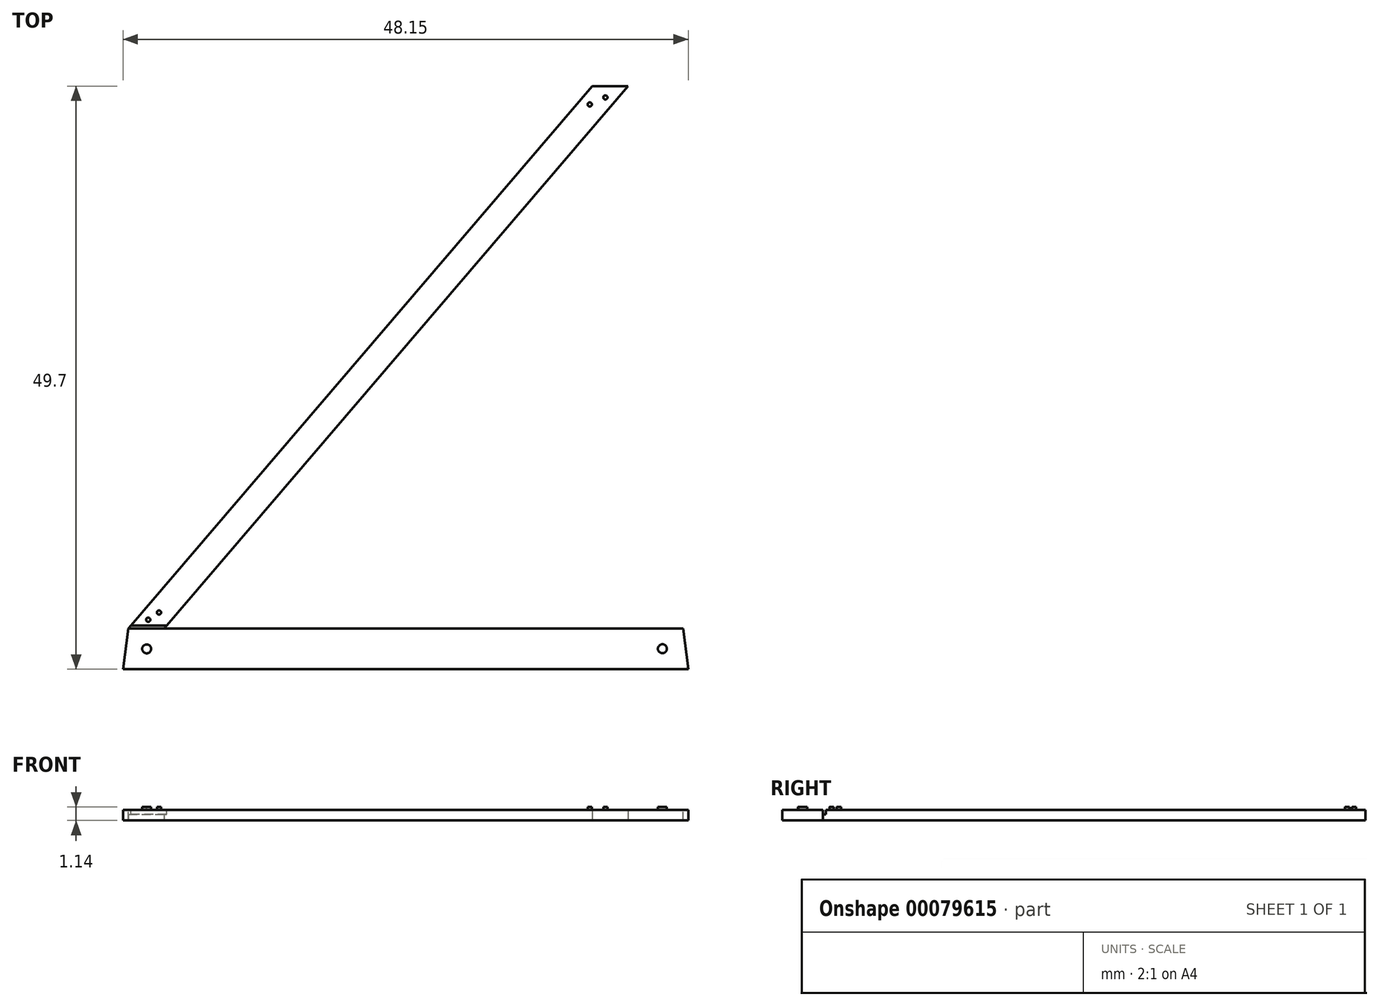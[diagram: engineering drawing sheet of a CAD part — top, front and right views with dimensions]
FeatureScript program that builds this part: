
annotation { "Feature Type Name" : "Feature", "Feature Type Description" : "" }
export const myFeature = defineFeature(function(context is Context, id is Id, definition is map)
    precondition{}
    {
        {
            var Q0;
            Q0=qCreatedBy(makeId("Top.planeOp"),FACE);
            var sketch = newSketch(context, id + "F0", { "sketchPlane" : qUnion([Q0])});
            skLineSegment(sketch, "E0.bottom", {"start": v(-26.81, -12.22) * mm, "end": v(-24.95, -12.22) * mm});
            skLineSegment(sketch, "E0.top", {"start": v(-26.81, -15.7) * mm, "end": v(23.99, -15.7) * mm});
            skLineSegment(sketch, "E0.left", {"start": v(-26.81, -12.22) * mm, "end": v(-26.81, -15.7) * mm});
            skLineSegment(sketch, "E0.right", {"start": v(23.99, -12.22) * mm, "end": v(23.99, -15.7) * mm});
            skLineSegment(sketch, "E1", {"start": v(-24.95, -12.22) * mm, "end": v(14.59, 34.01) * mm});
            skLineSegment(sketch, "E2", {"start": v(-21.9, -12.22) * mm, "end": v(17.64, 34.01) * mm});
            skLineSegment(sketch, "E3", {"start": v(14.59, 34.01) * mm, "end": v(17.64, 34.01) * mm});
            skLineSegment(sketch, "E4.trimOffspring", {"start": v(-21.9, -12.22) * mm, "end": v(23.99, -12.22) * mm});
            skSolve(sketch);
        }
        {
            var Q0;
            Q0=qSketchRegion(id+"F0",true);
            extrude(context, id + "F1", {"entities" : qUnion([Q0]), "depth" : 0.89 * mm});
        }
        {
            var Q0;
            Q0=makeQuery(id+"F1.opExtrude","CAP_FACE",FACE,{"disambiguationData":[OSD([sQuery(id+"F0.wireOp",EDGE,"E0.bottom"),sQuery(id+"F0.wireOp",EDGE,"E0.top"),sQuery(id+"F0.wireOp",EDGE,"E0.left"),sQuery(id+"F0.wireOp",EDGE,"E0.right"),sQuery(id+"F0.wireOp",EDGE,"E1"),sQuery(id+"F0.wireOp",EDGE,"E2"),sQuery(id+"F0.wireOp",EDGE,"E3"),sQuery(id+"F0.wireOp",EDGE,"E4.trimOffspring")])],"isStart":false});
            var sketch = newSketch(context, id + "F2", { "sketchPlane" : qUnion([Q0])});
            skLineSegment(sketch, "E5", {"start": v(-24.95, -12.22) * mm, "end": v(-21.9, -12.22) * mm});
            skLineSegment(sketch, "E6", {"start": v(-21.9, -12.22) * mm, "end": v(-21.68, -11.96) * mm});
            skLineSegment(sketch, "E7", {"start": v(-21.68, -11.96) * mm, "end": v(-24.73, -11.96) * mm});
            skLineSegment(sketch, "E8", {"start": v(-24.73, -11.96) * mm, "end": v(-24.95, -12.22) * mm});
            skSolve(sketch);
        }
        {
            var Q0;
            Q0=qSketchRegion(id+"F2",true);
            extrude(context, id + "F3", {"entities" : qUnion([Q0]), "operationType" : NewBodyOperationType.REMOVE, "oppositeDirection" : true, "depth" : 0.38 * mm});
        }
        {
            var Q0;
            {var subQ0=sQuery(id+"F0.wireOp",EDGE,"E1");var subQ1=sQuery(id+"F0.wireOp",EDGE,"E2");var subQ2=sQuery(id+"F0.wireOp",EDGE,"E3");Q0=makeQuery(id+"F3.boolean.opBoolean","SPLIT",FACE,{"disambiguationData":[TD([makeQuery(id+"F1.opExtrude","SWEPT_FACE",FACE,{"disambiguationData":[OSD([subQ0])]})])],"derivedFrom":makeQuery(id+"F1.opExtrude","CAP_FACE",FACE,{"disambiguationData":[OSD([sQuery(id+"F0.wireOp",EDGE,"E0.bottom"),sQuery(id+"F0.wireOp",EDGE,"E0.top"),sQuery(id+"F0.wireOp",EDGE,"E0.left"),sQuery(id+"F0.wireOp",EDGE,"E0.right"),subQ0,subQ1,subQ2,sQuery(id+"F0.wireOp",EDGE,"E4.trimOffspring")])],"isStart":false})});}
            var sketch = newSketch(context, id + "F4", { "sketchPlane" : qUnion([Q0])});
            skCircle(sketch, "E9", {"center": v(-23.25, -11.47) * mm, "radius": 0.18 * mm});
            skCircle(sketch, "E10", {"center": v(-22.34, -10.85) * mm, "radius": 0.18 * mm});
            skCircle(sketch, "E11", {"center": v(-23.38, -13.95) * mm, "radius": 0.38 * mm});
            skCircle(sketch, "E12", {"center": v(15.7, 33.05) * mm, "radius": 0.18 * mm});
            skCircle(sketch, "E13", {"center": v(14.37, 32.45) * mm, "radius": 0.18 * mm});
            skCircle(sketch, "E14", {"center": v(20.56, -13.94) * mm, "radius": 0.38 * mm});
            skSolve(sketch);
        }
        {
            var Q0;
            Q0=qSketchRegion(id+"F4",true);
            extrude(context, id + "F5", {"entities" : qUnion([Q0]), "operationType" : NewBodyOperationType.ADD, "depth" : 0.25 * mm});
        }
        {
            var Q0;
            {var subQ0=sQuery(id+"F0.wireOp",EDGE,"E0.right");var subQ1=sQuery(id+"F0.wireOp",EDGE,"E0.left");var subQ2=sQuery(id+"F0.wireOp",EDGE,"E0.top");var subQ3=sQuery(id+"F0.wireOp",EDGE,"E0.bottom");var subQ4=sQuery(id+"F0.wireOp",EDGE,"E4.trimOffspring");Q0=makeQuery(id+"F3.boolean.opBoolean","SPLIT",FACE,{"disambiguationData":[TD([makeQuery(id+"F1.opExtrude","SWEPT_FACE",FACE,{"disambiguationData":[OSD([subQ3])]})])],"derivedFrom":makeQuery(id+"F1.opExtrude","CAP_FACE",FACE,{"disambiguationData":[OSD([subQ3,subQ2,subQ1,subQ0,sQuery(id+"F0.wireOp",EDGE,"E1"),sQuery(id+"F0.wireOp",EDGE,"E2"),sQuery(id+"F0.wireOp",EDGE,"E3"),subQ4])],"isStart":false})});}
            var sketch = newSketch(context, id + "F6", { "sketchPlane" : qUnion([Q0])});
            skLineSegment(sketch, "E15", {"start": v(-24.96, -12.22) * mm, "end": v(-25.39, -15.7) * mm});
            skLineSegment(sketch, "E16", {"start": v(-24.96, -12.22) * mm, "end": v(-26.81, -12.22) * mm});
            skLineSegment(sketch, "E17", {"start": v(-26.81, -12.22) * mm, "end": v(-26.81, -15.7) * mm});
            skLineSegment(sketch, "E18", {"start": v(-26.81, -15.7) * mm, "end": v(-25.39, -15.7) * mm});
            skLineSegment(sketch, "E19", {"start": v(22.76, -15.7) * mm, "end": v(22.34, -12.22) * mm});
            skLineSegment(sketch, "E20", {"start": v(22.34, -12.22) * mm, "end": v(23.99, -12.22) * mm});
            skLineSegment(sketch, "E21", {"start": v(23.99, -12.22) * mm, "end": v(23.99, -15.7) * mm});
            skLineSegment(sketch, "E22", {"start": v(23.99, -15.7) * mm, "end": v(22.76, -15.7) * mm});
            skSolve(sketch);
        }
        {
            var Q0;
            Q0 = qSketchRegion(id + "F6", true);
            extrude(context, id + "F7", {"entities" : qUnion([Q0]), "operationType" : NewBodyOperationType.REMOVE, "oppositeDirection" : true, "depth" : 25.4 * mm});
        }
    });
